# Revit family: QF_Kelvinator_738310_KCHGM72F_3-Hinged_Glass_Door_Full_Height_Merchandiser_Freezer_cat
name_source: partatom
category: Specialty Equipment
units: mm (PartAtom-declared; Revit-internal decimal feet)

## family parameters
Always vertical = Yes
Cut with Voids When Loaded = No
Part Type = Normal
Room Calculation Point = No
Round Connector Dimension = Use Diameter
Shared = No
Work Plane-Based = No

## types (1)
- QF_Kelvinator_738310_KCHGM72F_3-Hinged_Glass_Door_Full_Height_Merchandiser_Freezer_cat
    Apparent Power = 0 VA
    Conn Conduit = Yes
    Conn Plug = L14-20P
    Cycle = 60 Hz
    Default Elevation = 0 "
    Depth = 31.89 "
    Description = 3-Hinged Glass Door Full Height Merchandiser Freezer
    Elec Conn Connection Height = 0 "
    Elec Conn RI Height = 0 "
    FL Amps = 9 A
    Foodservice Equipment Identifier = Yes
    HP = 1 1/2
    Height = 83.701 "
    Identify Quantity as Lot = Yes
    Item Number = 738310
    Length = 80.984 "
    Manufacturer = Kelvinator Commercial
    Max Overcurrent Protection = 0 A
    Min Ckt Ampacity = 0 A
    Model = 738310 (KCHGM72F)
    Number of Poles = 2
    Phase = 1
    Volts = 115 V
    Watts = 1035 W
    Weight in Pounds = 694.456

## geometry (parser evidence)
native form markers: Sweep x7
no freeform markers — native parametric forms only
